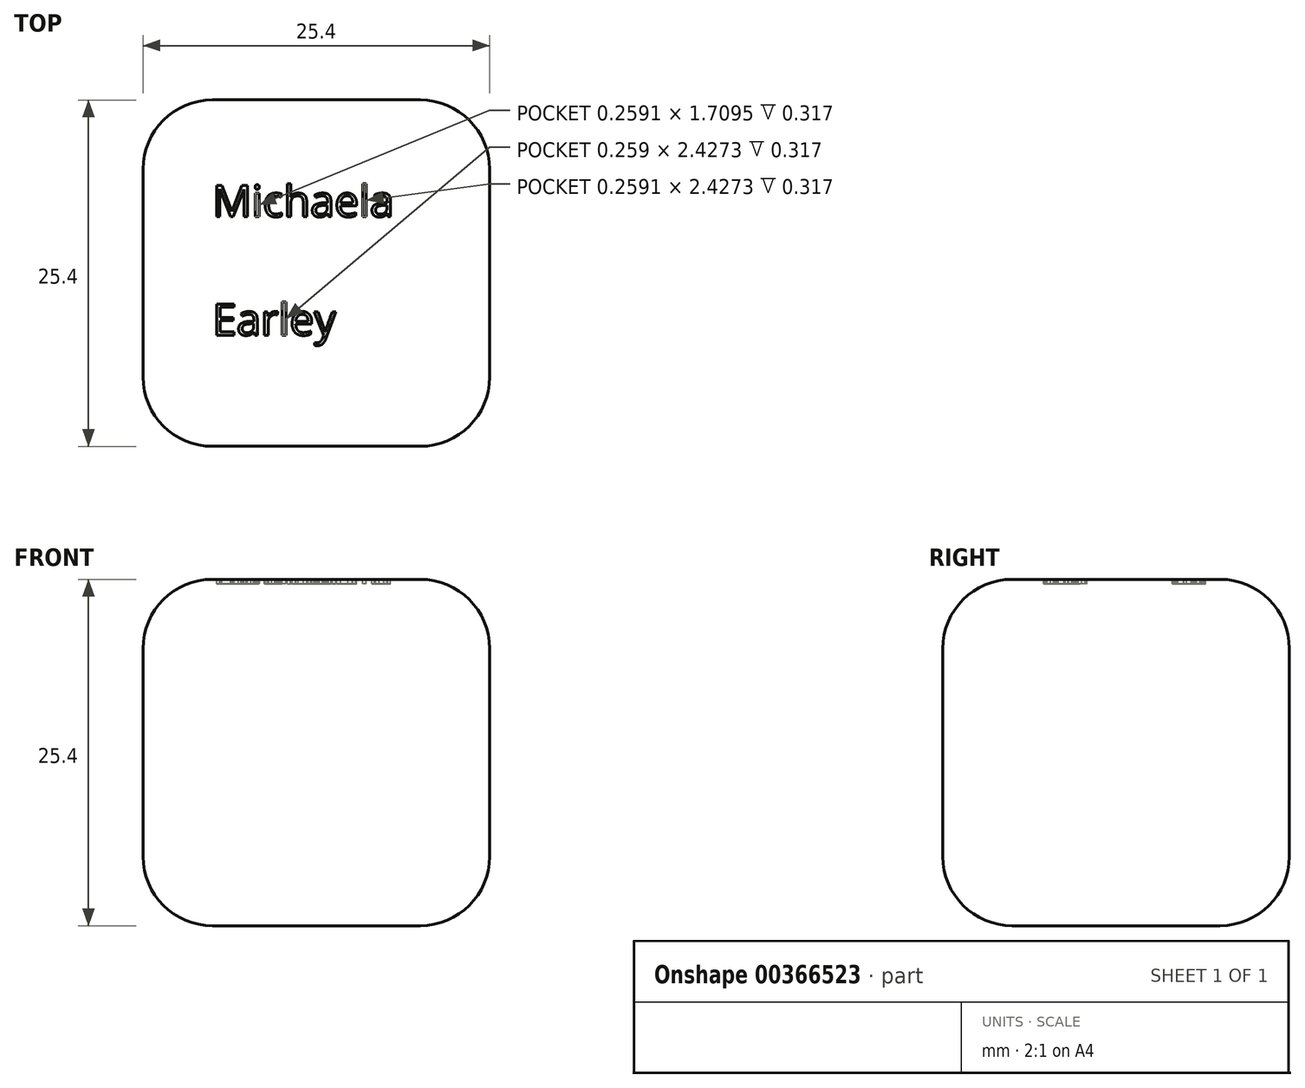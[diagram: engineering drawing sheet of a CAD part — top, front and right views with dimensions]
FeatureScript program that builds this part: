
annotation { "Feature Type Name" : "Feature", "Feature Type Description" : "" }
export const myFeature = defineFeature(function(context is Context, id is Id, definition is map)
    precondition{}
    {
        {
            var Q0;
            Q0=qCreatedBy(makeId("Top.planeOp"),FACE);
            var sketch = newSketch(context, id + "F0", { "sketchPlane" : qUnion([Q0])});
            skLineSegment(sketch, "E0", {"start": v(19.5, 31.84) * mm, "end": v(19.5, 6.44) * mm});
            skLineSegment(sketch, "E1", {"start": v(19.5, 6.44) * mm, "end": v(-5.9, 6.44) * mm});
            skLineSegment(sketch, "E2", {"start": v(-5.9, 6.44) * mm, "end": v(-5.9, 31.84) * mm});
            skLineSegment(sketch, "E3", {"start": v(-5.9, 31.84) * mm, "end": v(19.5, 31.84) * mm});
            skSolve(sketch);
        }
        {
            var Q0;
            Q0 = qSketchRegion(id + "F0", true);
            extrude(context, id + "F1", {"entities" : qUnion([Q0]), "depth" : 25.4 * mm});
        }
        {
            var Q0;
            Q0=makeQuery(id+"F1.opExtrude","CAP_EDGE",EDGE,{"disambiguationData":[OSD([sQuery(id+"F0.wireOp",EDGE,"E2")])],"isStart":false});
            var Q1;
            Q1=makeQuery(id+"F1.opExtrude","CAP_EDGE",EDGE,{"disambiguationData":[OSD([sQuery(id+"F0.wireOp",EDGE,"E3")])],"isStart":false});
            var Q2;
            Q2=makeQuery(id+"F1.opExtrude","SWEPT_EDGE",EDGE,{"disambiguationData":[OSD([sQuery(id+"F0.wireOp",EDGE,"E2"),sQuery(id+"F0.wireOp",EDGE,"E3")])]});
            var Q3;
            Q3=makeQuery(id+"F1.opExtrude","CAP_EDGE",EDGE,{"disambiguationData":[OSD([sQuery(id+"F0.wireOp",EDGE,"E3")])],"isStart":true});
            var Q4;
            Q4=makeQuery(id+"F1.opExtrude","SWEPT_EDGE",EDGE,{"disambiguationData":[OSD([sQuery(id+"F0.wireOp",EDGE,"E0"),sQuery(id+"F0.wireOp",EDGE,"E3")])]});
            var Q5;
            Q5=makeQuery(id+"F1.opExtrude","CAP_EDGE",EDGE,{"disambiguationData":[OSD([sQuery(id+"F0.wireOp",EDGE,"E0")])],"isStart":true});
            fillet(context, id + "F2", {"entities" : qUnion([Q0, Q1, Q2, Q3, Q4, Q5]), "radius" : 5.08 * mm, "tangentPropagation" : true, "allowEdgeOverflow" : false});
        }
        {
            var Q0;
            {var subQ0=sQuery(id+"F0.wireOp",EDGE,"E3");Q0=makeQuery(id+"F2.opFillet","BLEND_EDGE",EDGE,{"blendedFrom":[makeQuery(id+"F1.opExtrude","SWEPT_EDGE",EDGE,{"disambiguationData":[OSD([sQuery(id+"F0.wireOp",EDGE,"E2"),subQ0])]}),makeQuery(id+"F1.opExtrude","CAP_EDGE",EDGE,{"disambiguationData":[OSD([subQ0])],"isStart":true})],"blendedInto":[]});}
            var Q1;
            {var subQ0=sQuery(id+"F0.wireOp",EDGE,"E3");Q1=makeQuery(id+"F2.opFillet","BLEND_EDGE",EDGE,{"blendedFrom":[makeQuery(id+"F1.opExtrude","SWEPT_EDGE",EDGE,{"disambiguationData":[OSD([sQuery(id+"F0.wireOp",EDGE,"E2"),subQ0])]}),makeQuery(id+"F1.opExtrude","SWEPT_FACE",FACE,{"disambiguationData":[OSD([subQ0])]})],"blendedInto":[makeQuery(id+"F1.opExtrude","SWEPT_FACE",FACE,{"disambiguationData":[OSD([subQ0])]})]});}
            var Q2;
            {var subQ0=sQuery(id+"F0.wireOp",EDGE,"E3");Q2=makeQuery(id+"F2.opFillet","BLEND_EDGE",EDGE,{"blendedFrom":[makeQuery(id+"F1.opExtrude","SWEPT_EDGE",EDGE,{"disambiguationData":[OSD([sQuery(id+"F0.wireOp",EDGE,"E0"),subQ0])]}),makeQuery(id+"F1.opExtrude","CAP_EDGE",EDGE,{"disambiguationData":[OSD([subQ0])],"isStart":false})],"blendedInto":[]});}
            fillet(context, id + "F3", {"entities" : qUnion([Q0, Q1, Q2]), "radius" : 5.08 * mm, "tangentPropagation" : true, "allowEdgeOverflow" : false});
        }
        {
            var Q0;
            Q0=makeQuery(id+"F1.opExtrude","CAP_EDGE",EDGE,{"disambiguationData":[OSD([sQuery(id+"F0.wireOp",EDGE,"E1")])],"isStart":true});
            fillet(context, id + "F4", {"entities" : qUnion([Q0]), "radius" : 5.08 * mm, "tangentPropagation" : true, "allowEdgeOverflow" : false});
        }
        {
            var Q0;
            Q0=makeQuery(id+"F1.opExtrude","CAP_FACE",FACE,{"disambiguationData":[OSD([sQuery(id+"F0.wireOp",EDGE,"E0"),sQuery(id+"F0.wireOp",EDGE,"E1"),sQuery(id+"F0.wireOp",EDGE,"E2"),sQuery(id+"F0.wireOp",EDGE,"E3")])],"isStart":false});
            var sketch = newSketch(context, id + "F5", { "sketchPlane" : qUnion([Q0])});
            skText(sketch, "E4", { "text": "Michaela\n\nEarley\n", "fontName": "OpenSans-Regular.ttf"});
            const initialGuessF5  = {"E4": [-0.00083, 0.02328, 1, 0, 0.0023]};
            skSetInitialGuess(sketch, initialGuessF5);
            skSolve(sketch);
        }
        {
            var Q0;
            Q0 = qSketchRegion(id + "F5", true);
            extrude(context, id + "F6", {"entities" : qUnion([Q0]), "operationType" : NewBodyOperationType.REMOVE, "oppositeDirection" : true, "depth" : 0.32 * mm});
        }
    });
